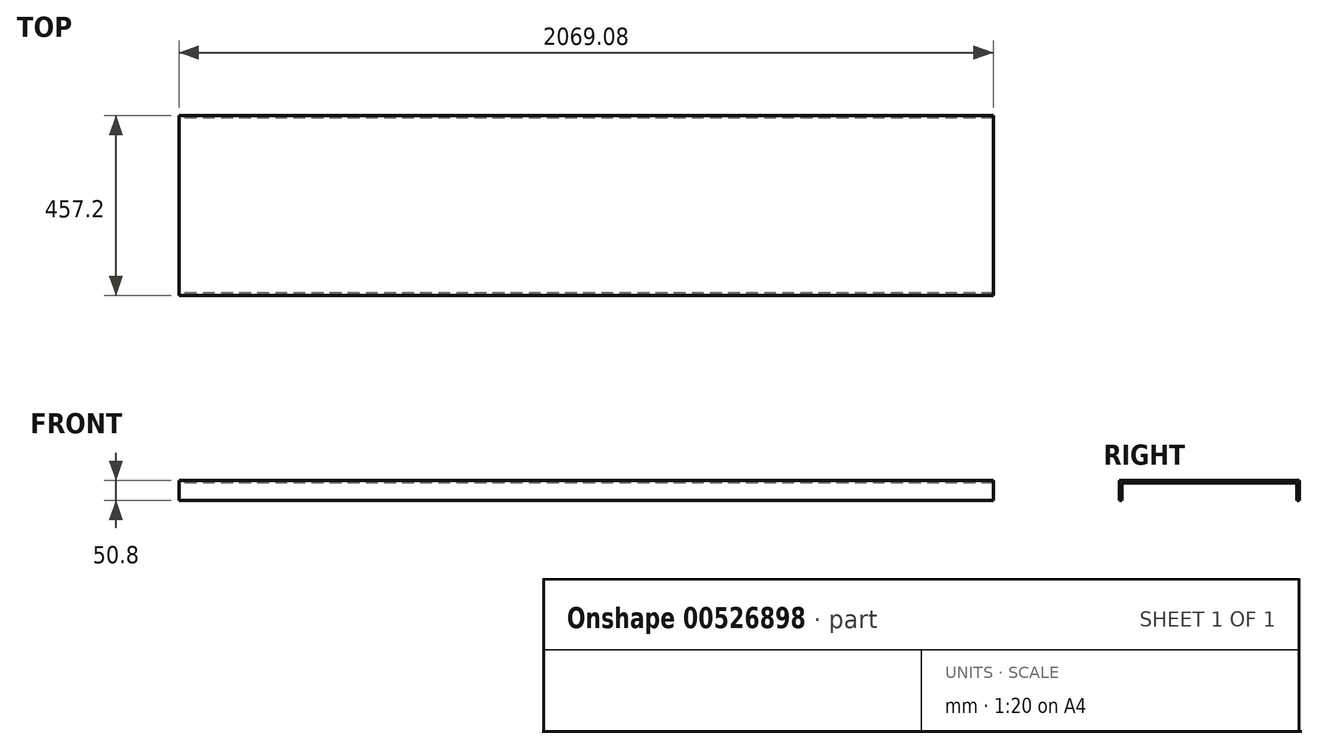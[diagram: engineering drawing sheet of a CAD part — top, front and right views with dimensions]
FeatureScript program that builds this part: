
annotation { "Feature Type Name" : "Feature", "Feature Type Description" : "" }
export const myFeature = defineFeature(function(context is Context, id is Id, definition is map)
    precondition{}
    {
        {
            var Q0;
            Q0=qCreatedBy(makeId("Right.planeOp"),FACE);
            var sketch = newSketch(context, id + "F0", { "sketchPlane" : qUnion([Q0])});
            skLineSegment(sketch, "E0", {"start": v(0, 0) * mm, "end": v(228.6, 0) * mm});
            skLineSegment(sketch, "E1", {"start": v(228.6, 0) * mm, "end": v(228.6, -50.8) * mm});
            skLineSegment(sketch, "E2", {"start": v(228.6, -50.8) * mm, "end": v(222.25, -50.8) * mm});
            skLineSegment(sketch, "E3", {"start": v(222.25, -50.8) * mm, "end": v(222.25, -6.35) * mm});
            skLineSegment(sketch, "E4", {"start": v(222.25, -6.35) * mm, "end": v(0, -6.35) * mm});
            skLineSegment(sketch, "E5", {"start": v(0, -6.35) * mm, "end": v(0, 0) * mm});
            skLineSegment(sketch, "E6.MirrorCS", {"start": v(0, 0) * mm, "end": v(-228.6, 0) * mm});
            skLineSegment(sketch, "E7.MirrorCS", {"start": v(-228.6, 0) * mm, "end": v(-228.6, -50.8) * mm});
            skLineSegment(sketch, "E8.MirrorCS", {"start": v(-222.25, -50.8) * mm, "end": v(-222.25, -6.35) * mm});
            skLineSegment(sketch, "E9.MirrorCS", {"start": v(-222.25, -6.35) * mm, "end": v(0, -6.35) * mm});
            skLineSegment(sketch, "E10.MirrorCS", {"start": v(-228.6, -50.8) * mm, "end": v(-222.25, -50.8) * mm});
            skSolve(sketch);
        }
        {
            var Q0;
            Q0 = qSketchRegion(id + "F0", true);
            extrude(context, id + "F1", {"entities" : qUnion([Q0]), "depth" : 2069.08 * mm, "offsetDistance" : 25.4 * mm});
        }
    });
